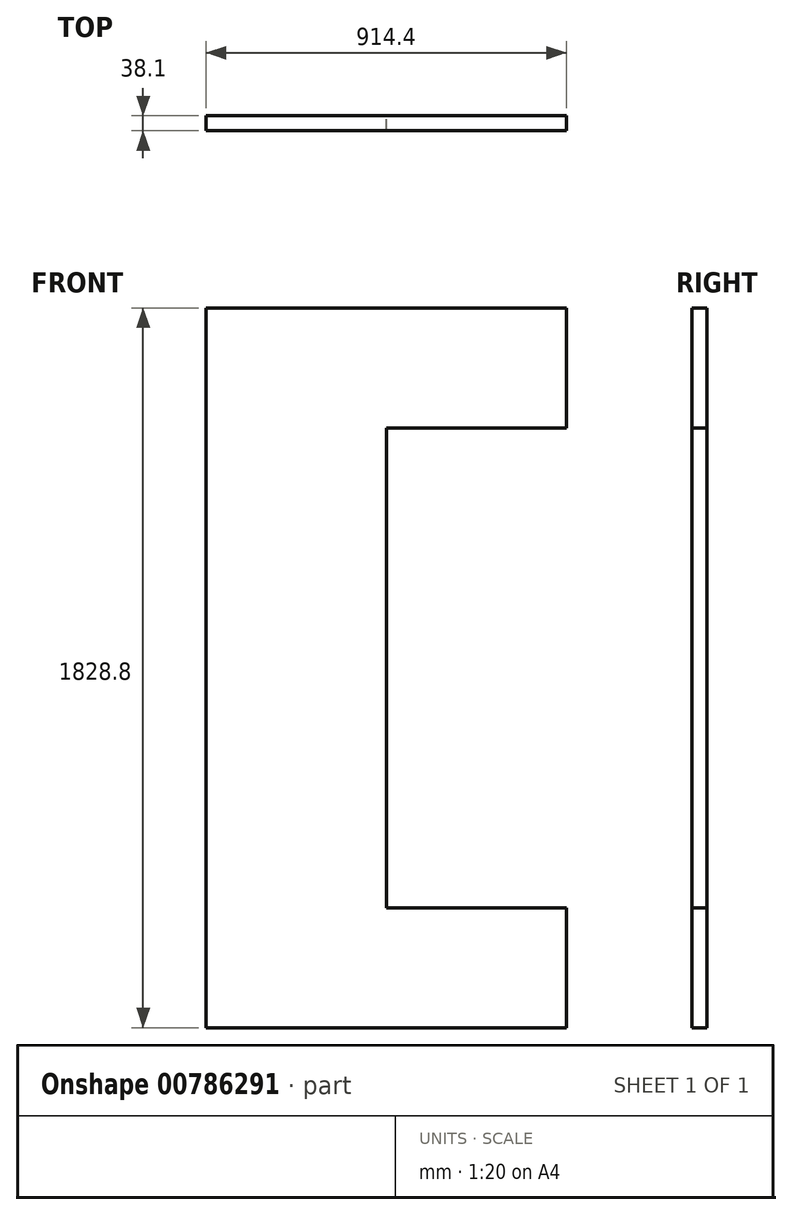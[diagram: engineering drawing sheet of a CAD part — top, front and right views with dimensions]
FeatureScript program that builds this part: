
annotation { "Feature Type Name" : "Feature", "Feature Type Description" : "" }
export const myFeature = defineFeature(function(context is Context, id is Id, definition is map)
    precondition{}
    {
        {
            var Q0;
            Q0=qCreatedBy(makeId("Front.planeOp"),FACE);
            var sketch = newSketch(context, id + "F0", { "sketchPlane" : qUnion([Q0])});
            skLineSegment(sketch, "E0.bottom", {"start": v(-457.2, 914.4) * mm, "end": v(457.2, 914.4) * mm});
            skLineSegment(sketch, "E0.top", {"start": v(-457.2, -914.4) * mm, "end": v(457.2, -914.4) * mm});
            skLineSegment(sketch, "E0.left", {"start": v(-457.2, 914.4) * mm, "end": v(-457.2, -914.4) * mm});
            skLineSegment(sketch, "E0.right", {"start": v(457.2, 914.4) * mm, "end": v(457.2, -914.4) * mm});
            skPoint(sketch, "E0.middle", {"position": v(0, 0) * mm});
            skLineSegment(sketch, "E1.top", {"start": v(0, -609.6) * mm, "end": v(0, -609.6) * mm});
            skLineSegment(sketch, "E1.left", {"start": v(0, 609.6) * mm, "end": v(0, -609.6) * mm});
            skLineSegment(sketch, "E2", {"start": v(0, 609.6) * mm, "end": v(457.2, 609.6) * mm});
            skLineSegment(sketch, "E3", {"start": v(0, -609.6) * mm, "end": v(457.2, -609.6) * mm});
            skSolve(sketch);
        }
        {
            var Q0;
            Q0=makeQuery(id+"F0.imprint","IMPRINT",FACE,{"disambiguationData":[TD([[makeQuery(id+"F0.imprint","IMPRINT",EDGE,{"derivedFrom":sQuery(id+"F0.wireOp",EDGE,"E0.bottom")}),-1.0]])]});
            extrude(context, id + "F1", {"entities" : qUnion([Q0]), "endBound" : BoundingType.SYMMETRIC, "depth" : 38.1 * mm, "offsetDistance" : 25.4 * mm});
        }
    });
